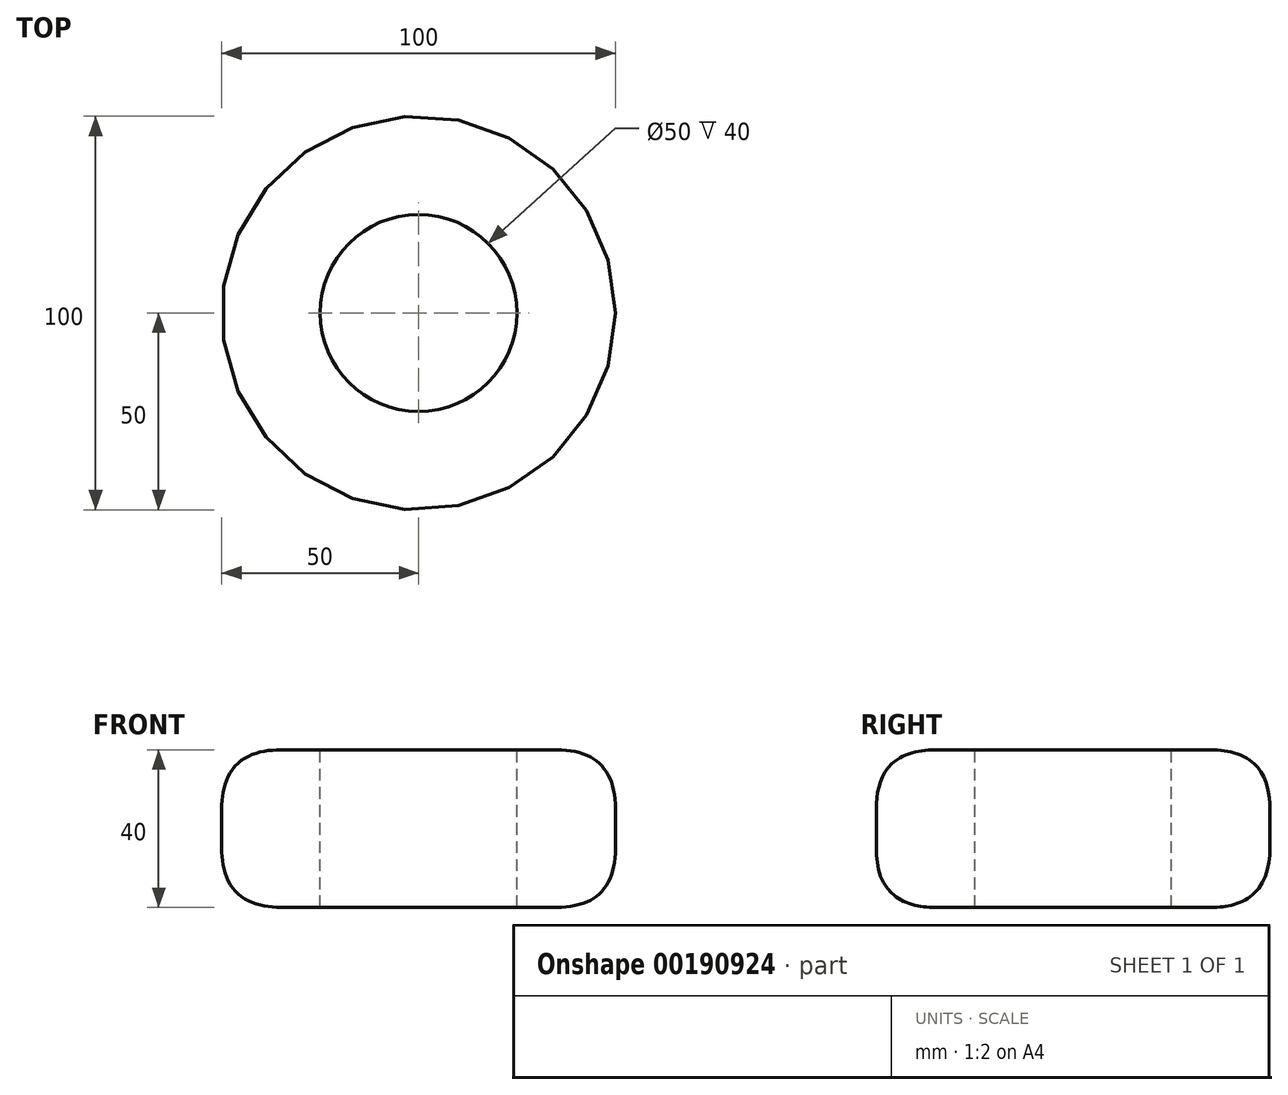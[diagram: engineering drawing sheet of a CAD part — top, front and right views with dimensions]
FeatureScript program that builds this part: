
annotation { "Feature Type Name" : "Feature", "Feature Type Description" : "" }
export const myFeature = defineFeature(function(context is Context, id is Id, definition is map)
    precondition{}
    {
        {
            var Q0;
            Q0=qCreatedBy(makeId("Top.planeOp"),FACE);
            var sketch = newSketch(context, id + "F0", { "sketchPlane" : qUnion([Q0])});
            skCircle(sketch, "E0", {"center": v(0, 0) * mm, "radius": 50 * mm});
            skSolve(sketch);
        }
        {
            var Q0;
            Q0=qSketchRegion(id+"F0",true);
            extrude(context, id + "F1", {"entities" : qUnion([Q0]), "depth" : 40 * mm, "offsetDistance" : 25 * mm, "symmetric" : true});
        }
        {
            var Q0;
            Q0=makeQuery(id+"F1.opExtrude","SWEPT_FACE",FACE,{"disambiguationData":[OSD([sQuery(id+"F0.wireOp",EDGE,"E0")])]});
            fillet(context, id + "F2", {"entities" : qUnion([Q0]), "radius" : 15 * mm, "tangentPropagation" : true, "rho" : 0.5, "crossSection" : FilletCrossSection.CONIC, "allowEdgeOverflow" : false});
        }
        {
            var Q0;
            Q0=makeQuery(id+"F1.opExtrude","CAP_FACE",FACE,{"disambiguationData":[OSD([sQuery(id+"F0.wireOp",EDGE,"E0")])],"isStart":false});
            var sketch = newSketch(context, id + "F3", { "sketchPlane" : qUnion([Q0])});
            skCircle(sketch, "E1", {"center": v(0, 0) * mm, "radius": 25 * mm});
            skSolve(sketch);
        }
        {
            var Q0;
            Q0 = qSketchRegion(id + "F3", true);
            extrude(context, id + "F4", {"entities" : qUnion([Q0]), "operationType" : NewBodyOperationType.REMOVE, "endBound" : BoundingType.THROUGH_ALL, "oppositeDirection" : true, "depth" : 25 * mm, "offsetDistance" : 25 * mm});
        }
    });
